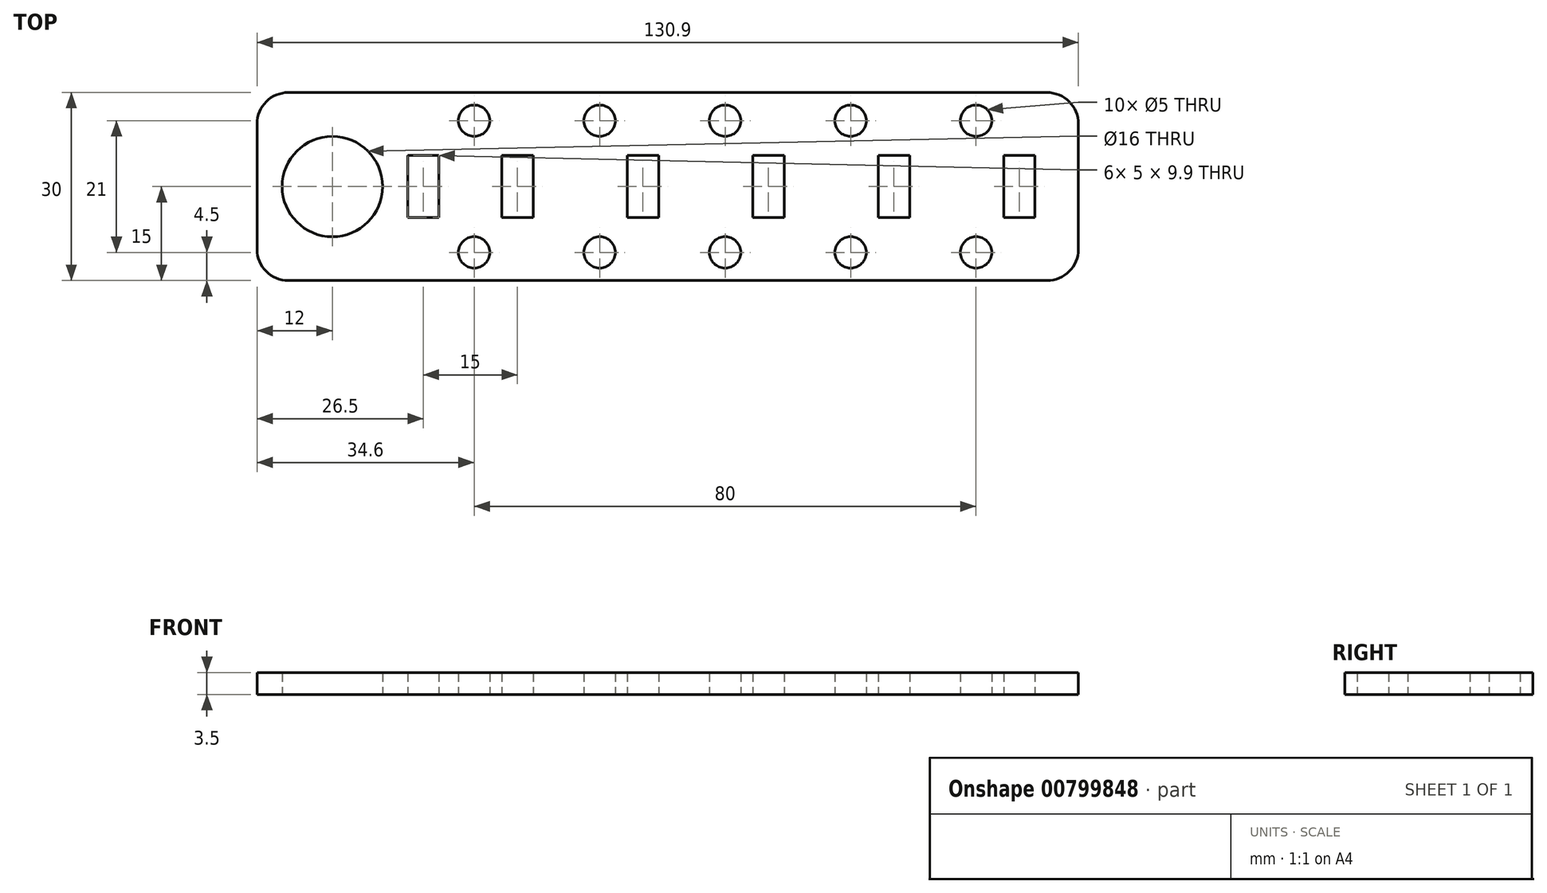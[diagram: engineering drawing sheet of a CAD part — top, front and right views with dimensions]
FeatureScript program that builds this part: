
annotation { "Feature Type Name" : "Feature", "Feature Type Description" : "" }
export const myFeature = defineFeature(function(context is Context, id is Id, definition is map)
    precondition{}
    {
        {
            var Q0;
            Q0=qCreatedBy(makeId("Top.planeOp"),FACE);
            var sketch = newSketch(context, id + "F0", { "sketchPlane" : qUnion([Q0])});
            skLineSegment(sketch, "E0.bottom", {"start": v(0, 0) * mm, "end": v(-125.9, 0) * mm});
            skLineSegment(sketch, "E0.top", {"start": v(0, -30) * mm, "end": v(-130.9, -30) * mm});
            skLineSegment(sketch, "E0.left", {"start": v(0, -5) * mm, "end": v(0, -25) * mm});
            skLineSegment(sketch, "E0.right", {"start": v(-130.9, -5) * mm, "end": v(-130.9, -25) * mm});
            skLineSegment(sketch, "E1", {"start": v(-130.9, -15) * mm, "end": v(-126.9, -15) * mm, "construction": true});
            skLineSegment(sketch, "E2", {"start": v(-126.9, -15) * mm, "end": v(-118.9, -15) * mm, "construction": true});
            skCircle(sketch, "E3", {"center": v(-118.9, -15) * mm, "radius": 8 * mm});
            skLineSegment(sketch, "E4.bottom", {"start": v(-106.9, -10.05) * mm, "end": v(-101.9, -10.05) * mm});
            skLineSegment(sketch, "E4.top", {"start": v(-106.9, -19.95) * mm, "end": v(-101.9, -19.95) * mm});
            skLineSegment(sketch, "E4.left", {"start": v(-106.9, -10.05) * mm, "end": v(-106.9, -19.95) * mm});
            skLineSegment(sketch, "E4.right", {"start": v(-101.9, -10.05) * mm, "end": v(-101.9, -19.95) * mm});
            skLineSegment(sketch, "E5", {"start": v(-118.9, -15) * mm, "end": v(-106.9, -15) * mm, "construction": true});
            skLineSegment(sketch, "E6", {"start": v(-101.9, -15) * mm, "end": v(-86.9, -15) * mm, "construction": true});
            skLineSegment(sketch, "E7", {"start": v(-106.9, -15) * mm, "end": v(-91.9, -15) * mm, "construction": true});
            skLineSegment(sketch, "E8.bottom", {"start": v(-91.9, -10.02) * mm, "end": v(-86.9, -10.02) * mm});
            skLineSegment(sketch, "E8.top", {"start": v(-91.9, -19.92) * mm, "end": v(-86.9, -19.92) * mm});
            skLineSegment(sketch, "E8.left", {"start": v(-91.9, -10.02) * mm, "end": v(-91.9, -19.92) * mm});
            skLineSegment(sketch, "E8.right", {"start": v(-86.9, -10.02) * mm, "end": v(-86.9, -19.92) * mm});
            skLineSegment(sketch, "E9.bottom", {"start": v(-71.9, -10.02) * mm, "end": v(-66.9, -10.02) * mm});
            skLineSegment(sketch, "E9.top", {"start": v(-71.9, -19.92) * mm, "end": v(-66.9, -19.92) * mm});
            skLineSegment(sketch, "E9.left", {"start": v(-71.9, -10.02) * mm, "end": v(-71.9, -19.92) * mm});
            skLineSegment(sketch, "E9.right", {"start": v(-66.9, -10.02) * mm, "end": v(-66.9, -19.92) * mm});
            skLineSegment(sketch, "E10.bottom", {"start": v(-51.9, -10.02) * mm, "end": v(-46.9, -10.02) * mm});
            skLineSegment(sketch, "E10.top", {"start": v(-51.9, -19.92) * mm, "end": v(-46.9, -19.92) * mm});
            skLineSegment(sketch, "E10.left", {"start": v(-51.9, -10.02) * mm, "end": v(-51.9, -19.92) * mm});
            skLineSegment(sketch, "E10.right", {"start": v(-46.9, -10.02) * mm, "end": v(-46.9, -19.92) * mm});
            skLineSegment(sketch, "E11.bottom", {"start": v(-31.9, -10.02) * mm, "end": v(-26.9, -10.02) * mm});
            skLineSegment(sketch, "E11.top", {"start": v(-31.9, -19.92) * mm, "end": v(-26.9, -19.92) * mm});
            skLineSegment(sketch, "E11.left", {"start": v(-31.9, -10.02) * mm, "end": v(-31.9, -19.92) * mm});
            skLineSegment(sketch, "E11.right", {"start": v(-26.9, -10.02) * mm, "end": v(-26.9, -19.92) * mm});
            skLineSegment(sketch, "E12.bottom", {"start": v(-11.9, -10.02) * mm, "end": v(-6.9, -10.02) * mm});
            skLineSegment(sketch, "E12.top", {"start": v(-11.9, -19.92) * mm, "end": v(-6.9, -19.92) * mm});
            skLineSegment(sketch, "E12.left", {"start": v(-11.9, -10.02) * mm, "end": v(-11.9, -19.92) * mm});
            skLineSegment(sketch, "E12.right", {"start": v(-6.9, -10.02) * mm, "end": v(-6.9, -19.92) * mm});
            skLineSegment(sketch, "E13", {"start": v(-5, 0) * mm, "end": v(-16.3, 0) * mm, "construction": true});
            skLineSegment(sketch, "E14", {"start": v(-16.3, 0) * mm, "end": v(-16.3, -2) * mm, "construction": true});
            skLineSegment(sketch, "E15", {"start": v(-16.3, -2) * mm, "end": v(-16.3, -4.5) * mm, "construction": true});
            skCircle(sketch, "E16", {"center": v(-16.3, -4.5) * mm, "radius": 2.5 * mm});
            skLineSegment(sketch, "E17", {"start": v(-16.3, -4.5) * mm, "end": v(-36.3, -4.5) * mm, "construction": true});
            skLineSegment(sketch, "E18", {"start": v(-36.3, -4.5) * mm, "end": v(-56.3, -4.5) * mm, "construction": true});
            skLineSegment(sketch, "E19", {"start": v(-56.3, -4.5) * mm, "end": v(-76.3, -4.5) * mm, "construction": true});
            skCircle(sketch, "E20", {"center": v(-36.3, -4.5) * mm, "radius": 2.5 * mm});
            skCircle(sketch, "E21", {"center": v(-56.3, -4.5) * mm, "radius": 2.5 * mm});
            skCircle(sketch, "E22", {"center": v(-76.3, -4.5) * mm, "radius": 2.5 * mm});
            skLineSegment(sketch, "E23", {"start": v(-76.3, -4.5) * mm, "end": v(-96.3, -4.5) * mm, "construction": true});
            skCircle(sketch, "E24", {"center": v(-96.3, -4.5) * mm, "radius": 2.5 * mm});
            skLineSegment(sketch, "E25.MirrorCS", {"start": v(-16.3, -30) * mm, "end": v(-16.3, -28) * mm, "construction": true});
            skLineSegment(sketch, "E26.MirrorCS", {"start": v(0, -30) * mm, "end": v(-125.9, -30) * mm});
            skLineSegment(sketch, "E27.MirrorCS", {"start": v(-5, -30) * mm, "end": v(-16.3, -30) * mm, "construction": true});
            skLineSegment(sketch, "E28.MirrorCS", {"start": v(-16.3, -28) * mm, "end": v(-16.3, -25.5) * mm, "construction": true});
            skLineSegment(sketch, "E29.MirrorCS", {"start": v(-16.3, -25.5) * mm, "end": v(-36.3, -25.5) * mm, "construction": true});
            skCircle(sketch, "E30.MirrorC", {"center": v(-36.3, -25.5) * mm, "radius": 2.5 * mm});
            skCircle(sketch, "E31.MirrorC", {"center": v(-16.3, -25.5) * mm, "radius": 2.5 * mm});
            skCircle(sketch, "E32.MirrorC", {"center": v(-56.3, -25.5) * mm, "radius": 2.5 * mm});
            skLineSegment(sketch, "E33.MirrorCS", {"start": v(-36.3, -25.5) * mm, "end": v(-56.3, -25.5) * mm, "construction": true});
            skCircle(sketch, "E34.MirrorC", {"center": v(-96.3, -25.5) * mm, "radius": 2.5 * mm});
            skLineSegment(sketch, "E35.MirrorCS", {"start": v(-76.3, -25.5) * mm, "end": v(-96.3, -25.5) * mm, "construction": true});
            skLineSegment(sketch, "E36.MirrorCS", {"start": v(-56.3, -25.5) * mm, "end": v(-76.3, -25.5) * mm, "construction": true});
            skCircle(sketch, "E37.MirrorC", {"center": v(-76.3, -25.5) * mm, "radius": 2.5 * mm});
            skPoint(sketch, "E38.visualSharp", {"position": v(-130.9, 0) * mm});
            skArc(sketch, "E38.filletArc", {"start": v(-125.9, 0) * mm, "mid": v(-129.44, -1.46) * mm, "end": v(-130.9, -5) * mm});
            skPoint(sketch, "E39.visualSharp", {"position": v(-130.9, -30) * mm});
            skArc(sketch, "E39.filletArc", {"start": v(-130.9, -25) * mm, "mid": v(-129.44, -28.54) * mm, "end": v(-125.9, -30) * mm});
            skPoint(sketch, "E40.visualSharp", {"position": v(0, -30) * mm});
            skArc(sketch, "E40.filletArc", {"start": v(-5, -30) * mm, "mid": v(-1.46, -28.54) * mm, "end": v(0, -25) * mm});
            skPoint(sketch, "E41.visualSharp", {"position": v(0, 0) * mm});
            skArc(sketch, "E41.filletArc", {"start": v(0, -5) * mm, "mid": v(-1.46, -1.46) * mm, "end": v(-5, 0) * mm});
            skSolve(sketch);
        }
        {
            var Q0;
            Q0=makeQuery(id+"F0.imprint","IMPRINT",FACE,{"disambiguationData":[TD([[makeQuery(id+"F0.imprint","IMPRINT",EDGE,{"derivedFrom":sQuery(id+"F0.wireOp",EDGE,"E0.left")}),-1.0]])]});
            extrude(context, id + "F1", {"entities" : qUnion([Q0]), "depth" : 3.5 * mm, "offsetDistance" : 25 * mm});
        }
    });
